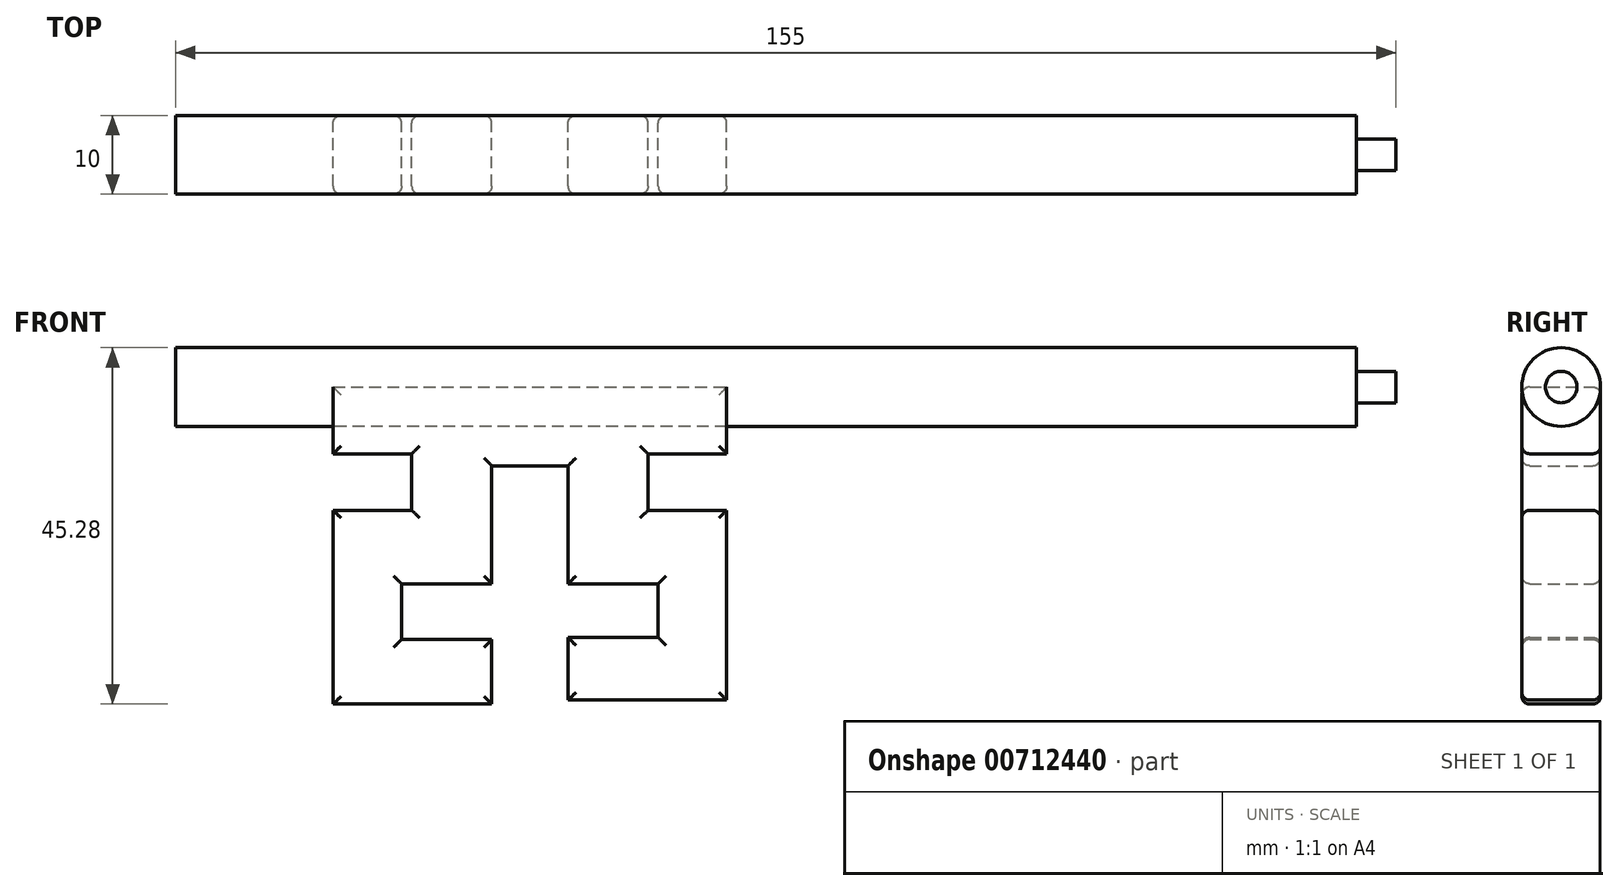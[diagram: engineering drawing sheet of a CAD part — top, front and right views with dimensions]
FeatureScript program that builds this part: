
annotation { "Feature Type Name" : "Feature", "Feature Type Description" : "" }
export const myFeature = defineFeature(function(context is Context, id is Id, definition is map)
    precondition{}
    {
        {
            var Q0;
            Q0=qCreatedBy(makeId("Front.planeOp"),FACE);
            var sketch = newSketch(context, id + "F0", { "sketchPlane" : qUnion([Q0])});
            skLineSegment(sketch, "E0", {"start": v(-4.85, -15.28) * mm, "end": v(-25, -15.28) * mm});
            skLineSegment(sketch, "E1", {"start": v(-25, -15.28) * mm, "end": v(-25, 9.33) * mm});
            skLineSegment(sketch, "E2", {"start": v(-25, 9.33) * mm, "end": v(-15, 9.33) * mm});
            skLineSegment(sketch, "E3", {"start": v(-15, 9.33) * mm, "end": v(-15, 16.51) * mm});
            skLineSegment(sketch, "E4", {"start": v(-15, 16.51) * mm, "end": v(-25, 16.51) * mm});
            skLineSegment(sketch, "E5", {"start": v(-25, 16.51) * mm, "end": v(-25, 25) * mm});
            skLineSegment(sketch, "E6", {"start": v(-25, 25) * mm, "end": v(25, 25) * mm});
            skLineSegment(sketch, "E7", {"start": v(25, 25) * mm, "end": v(25, 16.51) * mm});
            skLineSegment(sketch, "E8", {"start": v(25, 16.51) * mm, "end": v(15, 16.51) * mm});
            skLineSegment(sketch, "E9", {"start": v(15, 16.51) * mm, "end": v(15, 9.33) * mm});
            skLineSegment(sketch, "E10", {"start": v(15, 9.33) * mm, "end": v(25, 9.33) * mm});
            skLineSegment(sketch, "E11", {"start": v(25, 9.33) * mm, "end": v(25, -14.77) * mm});
            skLineSegment(sketch, "E12", {"start": v(25, -14.77) * mm, "end": v(4.85, -14.77) * mm});
            skLineSegment(sketch, "E13", {"start": v(4.85, -14.77) * mm, "end": v(4.85, -6.82) * mm});
            skLineSegment(sketch, "E14", {"start": v(4.85, -6.82) * mm, "end": v(16.3, -6.82) * mm});
            skLineSegment(sketch, "E15", {"start": v(16.3, -6.82) * mm, "end": v(16.3, 0) * mm});
            skLineSegment(sketch, "E16", {"start": v(16.3, 0) * mm, "end": v(4.85, 0) * mm});
            skLineSegment(sketch, "E17", {"start": v(4.85, 0) * mm, "end": v(4.85, 15) * mm});
            skLineSegment(sketch, "E18", {"start": v(4.85, 15) * mm, "end": v(-4.85, 15) * mm});
            skLineSegment(sketch, "E19", {"start": v(-4.85, 15) * mm, "end": v(-4.85, 0) * mm});
            skLineSegment(sketch, "E20", {"start": v(-4.85, 0) * mm, "end": v(-16.3, 0) * mm});
            skLineSegment(sketch, "E21", {"start": v(-4.85, -15.28) * mm, "end": v(-4.85, -7.08) * mm});
            skLineSegment(sketch, "E22", {"start": v(-4.85, -7.08) * mm, "end": v(-16.3, -7.08) * mm});
            skLineSegment(sketch, "E23", {"start": v(-16.3, -7.08) * mm, "end": v(-16.3, 0) * mm});
            skSolve(sketch);
        }
        {
            var Q0;
            Q0=qCreatedBy(makeId("Front.planeOp"),FACE);
            cPlane(context, id + "F1", {"entities" : qUnion([Q0]), "cplaneType" : CPlaneType.OFFSET, "offset" : 5 * mm, "width" : 150 * mm, "height" : 150 * mm});
        }
        {
            var Q0;
            Q0=makeQuery(id+"F0.imprint","IMPRINT",FACE,{"disambiguationData":[TD([[makeQuery(id+"F0.imprint","IMPRINT",EDGE,{"derivedFrom":sQuery(id+"F0.wireOp",EDGE,"E0")}),-1.0]])]});
            extrude(context, id + "F2", {"entities" : qUnion([Q0]), "depth" : 10 * mm, "offsetDistance" : 25 * mm});
        }
        {
            var Q0;
            Q0=qCreatedBy(id+"F1.planeOp",FACE);
            var sketch = newSketch(context, id + "F3", { "sketchPlane" : qUnion([Q0])});
            skLineSegment(sketch, "E24.bottom", {"start": v(-45, 30) * mm, "end": v(105, 30) * mm});
            skLineSegment(sketch, "E24.top", {"start": v(-45, 25) * mm, "end": v(105, 25) * mm});
            skLineSegment(sketch, "E24.left", {"start": v(-45, 30) * mm, "end": v(-45, 25) * mm});
            skLineSegment(sketch, "E25", {"start": v(105, 25) * mm, "end": v(110, 25) * mm});
            skLineSegment(sketch, "E26", {"start": v(110, 25) * mm, "end": v(110, 27) * mm});
            skLineSegment(sketch, "E27", {"start": v(110, 27) * mm, "end": v(105, 27) * mm});
            skLineSegment(sketch, "E28", {"start": v(105, 27) * mm, "end": v(105, 30) * mm});
            skSolve(sketch);
        }
        {
            var Q0;
            Q0=makeQuery(id+"F3.imprint","IMPRINT",FACE,{"disambiguationData":[TD([[makeQuery(id+"F3.imprint","IMPRINT",EDGE,{"derivedFrom":sQuery(id+"F3.wireOp",EDGE,"E24.bottom")}),-1.0]])]});
            var Q1;
            Q1=sQuery(id+"F3.wireOp",EDGE,"E24.top");
            revolve(context, id + "F4", {"surfaceOperationType" : NewSurfaceOperationType.NEW, "entities" : qUnion([Q0]), "axis" : qUnion([Q1]), "revolveType" : RevolveType.FULL});
        }
        {
            var Q0;
            Q0=makeQuery(id+"F2.opExtrude","CAP_FACE",FACE,{"disambiguationData":[OSD([sQuery(id+"F0.wireOp",EDGE,"E0"),sQuery(id+"F0.wireOp",EDGE,"E1"),sQuery(id+"F0.wireOp",EDGE,"E2"),sQuery(id+"F0.wireOp",EDGE,"E3"),sQuery(id+"F0.wireOp",EDGE,"E4"),sQuery(id+"F0.wireOp",EDGE,"E5"),sQuery(id+"F0.wireOp",EDGE,"E6"),sQuery(id+"F0.wireOp",EDGE,"E7"),sQuery(id+"F0.wireOp",EDGE,"E8"),sQuery(id+"F0.wireOp",EDGE,"E9"),sQuery(id+"F0.wireOp",EDGE,"E10"),sQuery(id+"F0.wireOp",EDGE,"E11"),sQuery(id+"F0.wireOp",EDGE,"E12"),sQuery(id+"F0.wireOp",EDGE,"E13"),sQuery(id+"F0.wireOp",EDGE,"E14"),sQuery(id+"F0.wireOp",EDGE,"E15"),sQuery(id+"F0.wireOp",EDGE,"E16"),sQuery(id+"F0.wireOp",EDGE,"E17"),sQuery(id+"F0.wireOp",EDGE,"E18"),sQuery(id+"F0.wireOp",EDGE,"E19"),sQuery(id+"F0.wireOp",EDGE,"E20"),sQuery(id+"F0.wireOp",EDGE,"E21"),sQuery(id+"F0.wireOp",EDGE,"E22"),sQuery(id+"F0.wireOp",EDGE,"E23")])],"isStart":false});
            fillet(context, id + "F5", {"entities" : qUnion([Q0]), "radius" : 1 * mm, "tangentPropagation" : true, "allowEdgeOverflow" : false});
        }
        {
            var Q0;
            Q0=makeQuery(id+"F2.opExtrude","CAP_FACE",FACE,{"disambiguationData":[OSD([sQuery(id+"F0.wireOp",EDGE,"E0"),sQuery(id+"F0.wireOp",EDGE,"E1"),sQuery(id+"F0.wireOp",EDGE,"E2"),sQuery(id+"F0.wireOp",EDGE,"E3"),sQuery(id+"F0.wireOp",EDGE,"E4"),sQuery(id+"F0.wireOp",EDGE,"E5"),sQuery(id+"F0.wireOp",EDGE,"E6"),sQuery(id+"F0.wireOp",EDGE,"E7"),sQuery(id+"F0.wireOp",EDGE,"E8"),sQuery(id+"F0.wireOp",EDGE,"E9"),sQuery(id+"F0.wireOp",EDGE,"E10"),sQuery(id+"F0.wireOp",EDGE,"E11"),sQuery(id+"F0.wireOp",EDGE,"E12"),sQuery(id+"F0.wireOp",EDGE,"E13"),sQuery(id+"F0.wireOp",EDGE,"E14"),sQuery(id+"F0.wireOp",EDGE,"E15"),sQuery(id+"F0.wireOp",EDGE,"E16"),sQuery(id+"F0.wireOp",EDGE,"E17"),sQuery(id+"F0.wireOp",EDGE,"E18"),sQuery(id+"F0.wireOp",EDGE,"E19"),sQuery(id+"F0.wireOp",EDGE,"E20"),sQuery(id+"F0.wireOp",EDGE,"E21"),sQuery(id+"F0.wireOp",EDGE,"E22"),sQuery(id+"F0.wireOp",EDGE,"E23")])],"isStart":true});
            fillet(context, id + "F6", {"entities" : qUnion([Q0]), "radius" : 1 * mm, "tangentPropagation" : true, "allowEdgeOverflow" : false});
        }
    });
